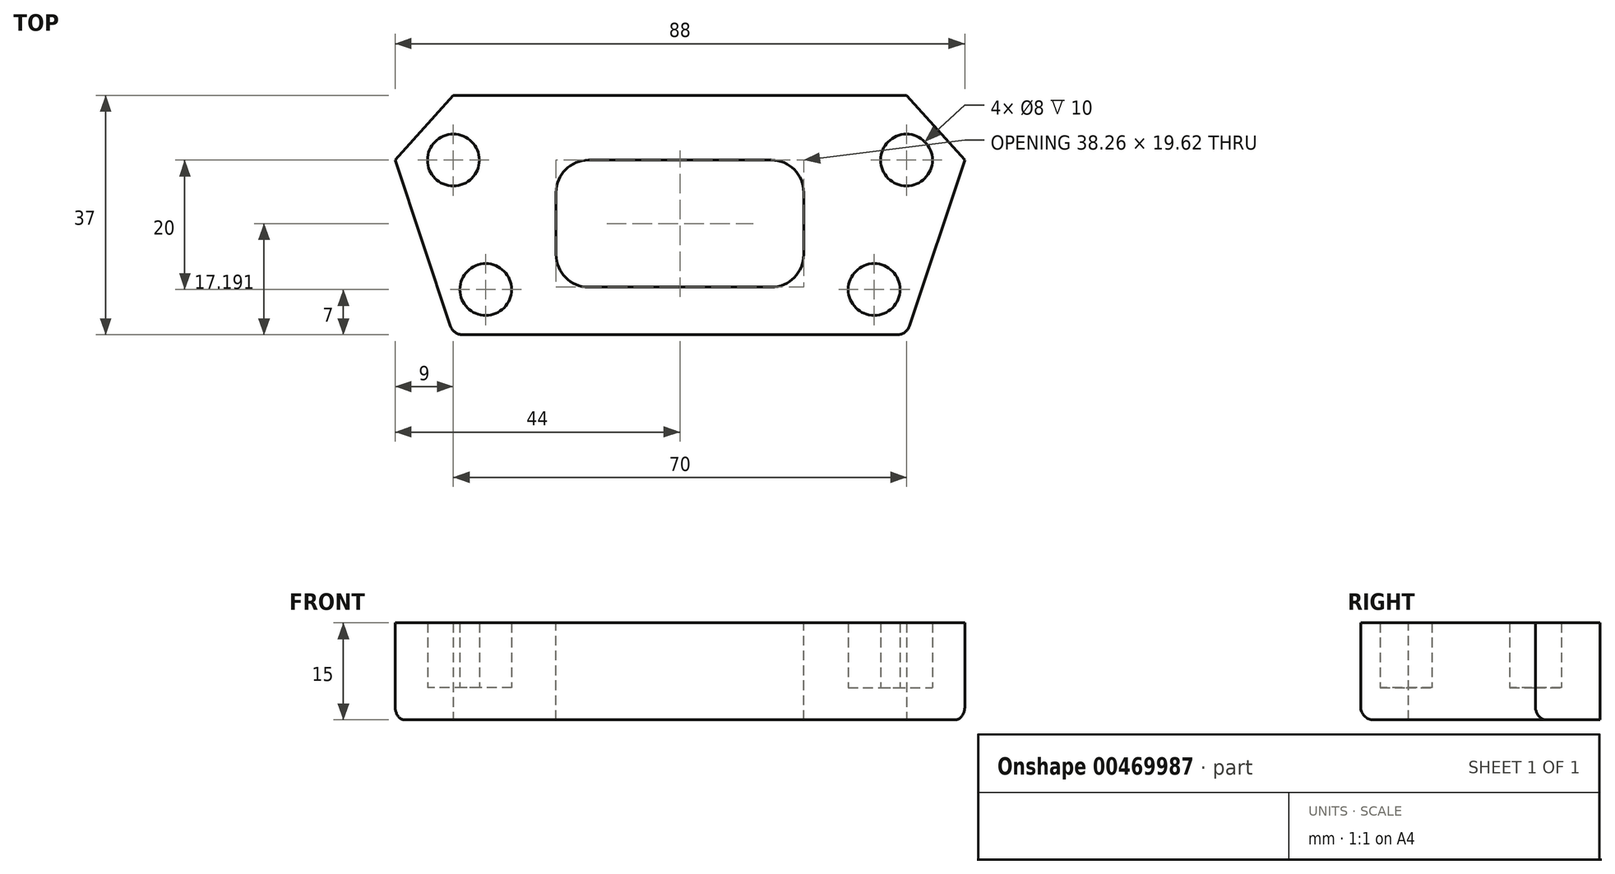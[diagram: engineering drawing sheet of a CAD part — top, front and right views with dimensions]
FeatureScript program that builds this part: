
annotation { "Feature Type Name" : "Feature", "Feature Type Description" : "" }
export const myFeature = defineFeature(function(context is Context, id is Id, definition is map)
    precondition{}
    {
        {
            var Q0;
            Q0=qCreatedBy(makeId("Top.planeOp"),FACE);
            var sketch = newSketch(context, id + "F0", { "sketchPlane" : qUnion([Q0])});
            skLineSegment(sketch, "E0", {"start": v(0, 0) * mm, "end": v(-35, 0) * mm, "construction": true});
            skCircle(sketch, "E1", {"center": v(-35, 0) * mm, "radius": 4 * mm, "construction": true});
            skLineSegment(sketch, "E2", {"start": v(0, 0) * mm, "end": v(0, -20) * mm, "construction": true});
            skLineSegment(sketch, "E3", {"start": v(0, -20) * mm, "end": v(-30, -20) * mm, "construction": true});
            skCircle(sketch, "E4", {"center": v(-30, -20) * mm, "radius": 4 * mm, "construction": true});
            skLineSegment(sketch, "E5", {"start": v(0, 0) * mm, "end": v(0, 10) * mm, "construction": true});
            skLineSegment(sketch, "E6.bottom", {"start": v(0, 10) * mm, "end": v(-44, 10) * mm, "construction": true});
            skLineSegment(sketch, "E6.top", {"start": v(0, -27) * mm, "end": v(-44, -27) * mm, "construction": true});
            skLineSegment(sketch, "E6.left", {"start": v(0, 10) * mm, "end": v(0, -27) * mm, "construction": true});
            skLineSegment(sketch, "E6.right", {"start": v(-44, 10) * mm, "end": v(-44, -27) * mm, "construction": true});
            skLineSegment(sketch, "E7.bottom", {"start": v(0, 10) * mm, "end": v(-22, 10) * mm, "construction": true});
            skLineSegment(sketch, "E7.top", {"start": v(0, -27) * mm, "end": v(-22, -27) * mm, "construction": true});
            skLineSegment(sketch, "E7.right", {"start": v(-22, 10) * mm, "end": v(-22, -27) * mm, "construction": true});
            skLineSegment(sketch, "E8", {"start": v(-35, 10) * mm, "end": v(-44, 0) * mm});
            skLineSegment(sketch, "E9", {"start": v(-44, 0) * mm, "end": v(-35, -27) * mm});
            skLineSegment(sketch, "E10", {"start": v(-35, -27) * mm, "end": v(-22, -27) * mm});
            skLineSegment(sketch, "E11", {"start": v(-22, -27) * mm, "end": v(0, -27) * mm});
            skLineSegment(sketch, "E12", {"start": v(0, 0) * mm, "end": v(0, -27) * mm});
            skCircle(sketch, "E13", {"center": v(-35, 0) * mm, "radius": 4 * mm});
            skCircle(sketch, "E14", {"center": v(-30, -20) * mm, "radius": 4 * mm});
            skLineSegment(sketch, "E15", {"start": v(-35, 10) * mm, "end": v(0, 10) * mm});
            skLineSegment(sketch, "E16", {"start": v(0, 0) * mm, "end": v(0, 10) * mm});
            skSolve(sketch);
        }
        {
            var Q0;
            Q0=makeQuery(id+"F0.imprint","IMPRINT",FACE,{"disambiguationData":[TD([[makeQuery(id+"F0.imprint","IMPRINT",EDGE,{"derivedFrom":sQuery(id+"F0.wireOp",EDGE,"E13")}),1.0]])]});
            var Q1;
            Q1=makeQuery(id+"F0.imprint","IMPRINT",FACE,{"disambiguationData":[TD([[makeQuery(id+"F0.imprint","IMPRINT",EDGE,{"derivedFrom":sQuery(id+"F0.wireOp",EDGE,"E14")}),1.0]])]});
            extrude(context, id + "F1", {"entities" : qUnion([Q0, Q1]), "depth" : 5 * mm, "offsetDistance" : 25 * mm});
        }
        {
            var Q0;
            Q0 = qSketchRegion(id + "F0", true);
            extrude(context, id + "F2", {"entities" : qUnion([Q0]), "depth" : 15 * mm, "offsetDistance" : 25 * mm});
        }
        {
            var Q0;
            Q0=makeQuery(id+"F2.opExtrude","SWEPT_BODY",BODY,{"disambiguationData":[OSD([sQuery(id+"F0.wireOp",EDGE,"E8"),sQuery(id+"F0.wireOp",EDGE,"E9"),sQuery(id+"F0.wireOp",EDGE,"E10"),sQuery(id+"F0.wireOp",EDGE,"E11"),sQuery(id+"F0.wireOp",EDGE,"E12"),sQuery(id+"F0.wireOp",EDGE,"E13"),sQuery(id+"F0.wireOp",EDGE,"E14"),sQuery(id+"F0.wireOp",EDGE,"E15"),sQuery(id+"F0.wireOp",EDGE,"E16")])]});
            var Q1;
            Q1=makeQuery(id+"F1.opExtrude","SWEPT_BODY",BODY,{"disambiguationData":[OSD([sQuery(id+"F0.wireOp",EDGE,"E13")])]});
            var Q2;
            Q2=makeQuery(id+"F1.opExtrude","SWEPT_BODY",BODY,{"disambiguationData":[OSD([sQuery(id+"F0.wireOp",EDGE,"E14")])]});
            var Q3;
            Q3=qCreatedBy(makeId("Right.planeOp"),FACE);
            mirror(context, id + "F3", {"operationType" : NewBodyOperationType.ADD, "entities" : qUnion([Q0, Q1, Q2]), "mirrorPlane" : qUnion([Q3])});
        }
        {
            var Q0;
            {var subQ0=makeQuery(id+"F2.opExtrude","CAP_EDGE",EDGE,{"disambiguationData":[OSD([sQuery(id+"F0.wireOp",EDGE,"E10"),sQuery(id+"F0.wireOp",EDGE,"E11")])],"isStart":true});Q0=makeQuery(id+"F3.boolean.opBoolean","MERGE",EDGE,{"derivedFrom":[subQ0,makeQuery(id+"F3.opPattern","COPY",EDGE,{"derivedFrom":subQ0,"instanceName":"1"})]});}
            var Q1;
            Q1=makeQuery(id+"F2.opExtrude","CAP_EDGE",EDGE,{"disambiguationData":[OSD([sQuery(id+"F0.wireOp",EDGE,"E9")])],"isStart":true});
            var Q2;
            Q2=makeQuery(id+"F3.opPattern","COPY",EDGE,{"derivedFrom":makeQuery(id+"F2.opExtrude","CAP_EDGE",EDGE,{"disambiguationData":[OSD([sQuery(id+"F0.wireOp",EDGE,"E9")])],"isStart":true}),"instanceName":"1"});
            var Q3;
            Q3=makeQuery(id+"F2.opExtrude","SWEPT_EDGE",EDGE,{"disambiguationData":[OSD([sQuery(id+"F0.wireOp",EDGE,"E9"),sQuery(id+"F0.wireOp",EDGE,"E10")])]});
            var Q4;
            Q4=makeQuery(id+"F3.opPattern","COPY",EDGE,{"derivedFrom":makeQuery(id+"F2.opExtrude","SWEPT_EDGE",EDGE,{"disambiguationData":[OSD([sQuery(id+"F0.wireOp",EDGE,"E9"),sQuery(id+"F0.wireOp",EDGE,"E10")])]}),"instanceName":"1"});
            fillet(context, id + "F4", {"entities" : qUnion([Q0, Q1, Q2, Q3, Q4]), "radius" : 2 * mm, "tangentPropagation" : true, "allowEdgeOverflow" : false});
        }
        {
            var Q0;
            {var subQ0=makeQuery(id+"F2.opExtrude","CAP_FACE",FACE,{"disambiguationData":[OSD([sQuery(id+"F0.wireOp",EDGE,"E8"),sQuery(id+"F0.wireOp",EDGE,"E9"),sQuery(id+"F0.wireOp",EDGE,"E10"),sQuery(id+"F0.wireOp",EDGE,"E11"),sQuery(id+"F0.wireOp",EDGE,"E12"),sQuery(id+"F0.wireOp",EDGE,"E13"),sQuery(id+"F0.wireOp",EDGE,"E14"),sQuery(id+"F0.wireOp",EDGE,"E15"),sQuery(id+"F0.wireOp",EDGE,"E16")])],"isStart":false});Q0=makeQuery(id+"F3.boolean.opBoolean","MERGE",FACE,{"derivedFrom":[subQ0,makeQuery(id+"F3.opPattern","COPY",FACE,{"derivedFrom":subQ0,"instanceName":"1"})]});}
            var sketch = newSketch(context, id + "F5", { "sketchPlane" : qUnion([Q0])});
            skLineSegment(sketch, "E17.bottom", {"start": v(-14.13, 0) * mm, "end": v(14.13, 0) * mm});
            skLineSegment(sketch, "E17.top", {"start": v(-14.13, -19.62) * mm, "end": v(14.13, -19.62) * mm});
            skLineSegment(sketch, "E17.left", {"start": v(-19.13, -5) * mm, "end": v(-19.13, -14.62) * mm});
            skLineSegment(sketch, "E17.right", {"start": v(19.13, -5) * mm, "end": v(19.13, -14.62) * mm});
            skPoint(sketch, "E17.middle", {"position": v(0, -9.8) * mm});
            skPoint(sketch, "E18.visualSharp", {"position": v(-19.13, 0) * mm});
            skArc(sketch, "E18.filletArc", {"start": v(-14.13, 0) * mm, "mid": v(-17.66, -1.46) * mm, "end": v(-19.13, -5) * mm});
            skPoint(sketch, "E19.visualSharp", {"position": v(19.13, 0) * mm});
            skArc(sketch, "E19.filletArc", {"start": v(19.13, -5) * mm, "mid": v(17.66, -1.46) * mm, "end": v(14.13, 0) * mm});
            skPoint(sketch, "E20.visualSharp", {"position": v(19.13, -19.62) * mm});
            skArc(sketch, "E20.filletArc", {"start": v(14.13, -19.62) * mm, "mid": v(17.66, -18.15) * mm, "end": v(19.13, -14.62) * mm});
            skPoint(sketch, "E21.visualSharp", {"position": v(-19.13, -19.62) * mm});
            skArc(sketch, "E21.filletArc", {"start": v(-19.13, -14.62) * mm, "mid": v(-17.66, -18.15) * mm, "end": v(-14.13, -19.62) * mm});
            skSolve(sketch);
        }
        {
            var Q0;
            Q0=makeQuery(id+"F5.imprint","IMPRINT",FACE,{"disambiguationData":[TD([[makeQuery(id+"F5.imprint","IMPRINT",EDGE,{"derivedFrom":sQuery(id+"F5.wireOp",EDGE,"E17.bottom")}),-1.0]])]});
            extrude(context, id + "F6", {"entities" : qUnion([Q0]), "operationType" : NewBodyOperationType.REMOVE, "oppositeDirection" : true, "depth" : 25 * mm, "offsetDistance" : 25 * mm});
        }
    });
